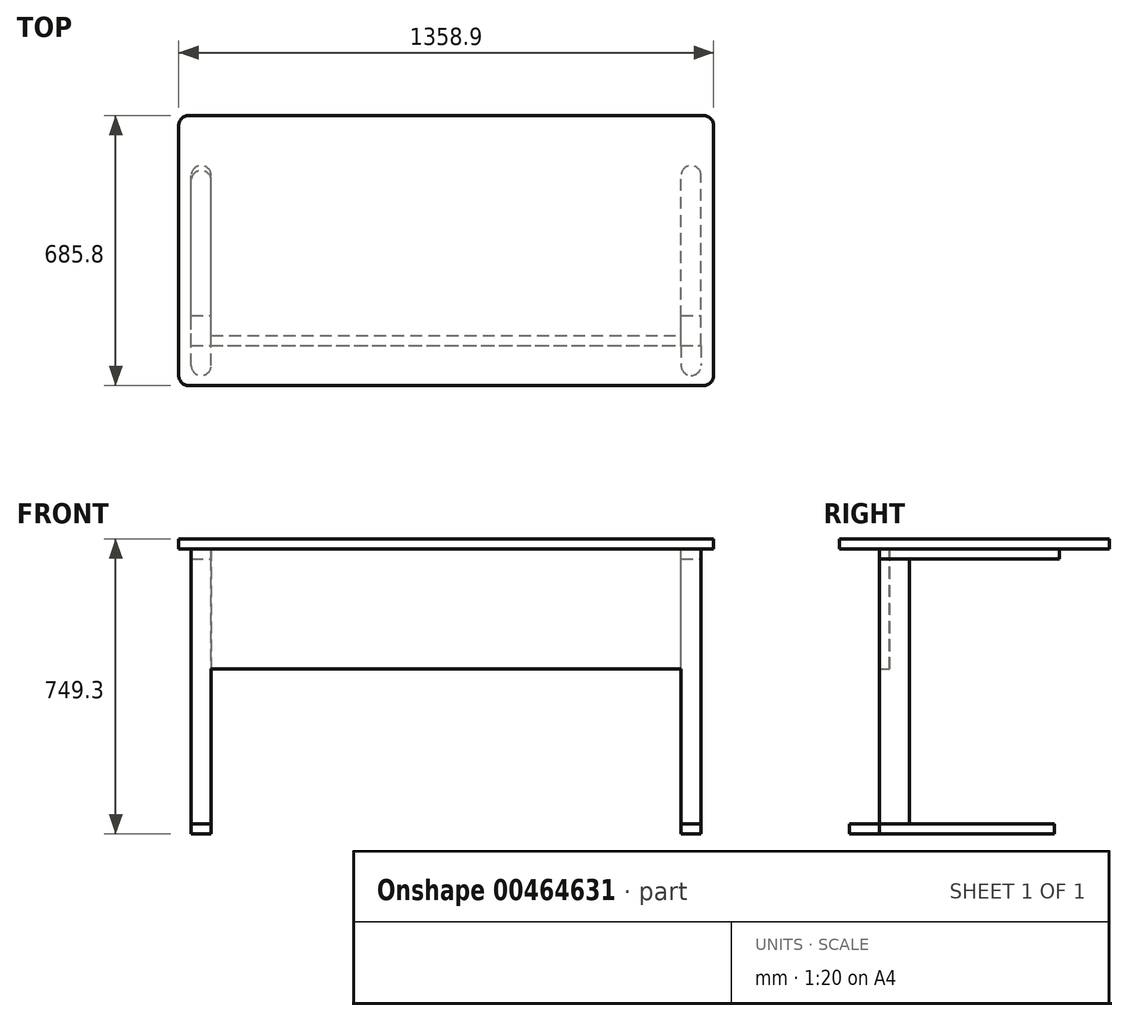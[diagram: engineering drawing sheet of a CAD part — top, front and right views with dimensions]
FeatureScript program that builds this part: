
annotation { "Feature Type Name" : "Feature", "Feature Type Description" : "" }
export const myFeature = defineFeature(function(context is Context, id is Id, definition is map)
    precondition{}
    {
        {
            var Q0;
            Q0=qCreatedBy(makeId("Top.planeOp"),FACE);
            var sketch = newSketch(context, id + "F0", { "sketchPlane" : qUnion([Q0])});
            skLineSegment(sketch, "E0.bottom", {"start": v(-592.93, 685.8) * mm, "end": v(715.17, 685.8) * mm});
            skLineSegment(sketch, "E0.top", {"start": v(-592.93, 0) * mm, "end": v(715.17, 0) * mm});
            skLineSegment(sketch, "E0.left", {"start": v(-618.33, 660.4) * mm, "end": v(-618.33, 25.4) * mm});
            skLineSegment(sketch, "E0.right", {"start": v(740.57, 660.4) * mm, "end": v(740.57, 25.4) * mm});
            skPoint(sketch, "E1.visualSharp", {"position": v(-618.33, 685.8) * mm});
            skArc(sketch, "E1.filletArc", {"start": v(-592.93, 685.8) * mm, "mid": v(-610.9, 678.36) * mm, "end": v(-618.33, 660.4) * mm});
            skPoint(sketch, "E2.visualSharp", {"position": v(740.57, 685.8) * mm});
            skArc(sketch, "E2.filletArc", {"start": v(740.57, 660.4) * mm, "mid": v(733.13, 678.36) * mm, "end": v(715.17, 685.8) * mm});
            skPoint(sketch, "E3.visualSharp", {"position": v(740.57, 0) * mm});
            skArc(sketch, "E3.filletArc", {"start": v(715.17, 0) * mm, "mid": v(733.13, 7.44) * mm, "end": v(740.57, 25.4) * mm});
            skPoint(sketch, "E4.visualSharp", {"position": v(-618.33, 0) * mm});
            skArc(sketch, "E4.filletArc", {"start": v(-618.33, 25.4) * mm, "mid": v(-610.9, 7.44) * mm, "end": v(-592.93, 0) * mm});
            skSolve(sketch);
        }
        {
            var Q0;
            Q0=makeQuery(id+"F0.imprint","IMPRINT",FACE,{"disambiguationData":[TD([[makeQuery(id+"F0.imprint","IMPRINT",EDGE,{"derivedFrom":sQuery(id+"F0.wireOp",EDGE,"E0.bottom")}),-1.0]])]});
            extrude(context, id + "F1", {"entities" : qUnion([Q0]), "depth" : 25.4 * mm});
        }
        {
            var Q0;
            Q0=makeQuery(id+"F1.opExtrude","CAP_FACE",FACE,{"disambiguationData":[OSD([sQuery(id+"F0.wireOp",EDGE,"E0.bottom"),sQuery(id+"F0.wireOp",EDGE,"E0.top"),sQuery(id+"F0.wireOp",EDGE,"E0.left"),sQuery(id+"F0.wireOp",EDGE,"E0.right"),sQuery(id+"F0.wireOp",EDGE,"E1.filletArc"),sQuery(id+"F0.wireOp",EDGE,"E2.filletArc"),sQuery(id+"F0.wireOp",EDGE,"E3.filletArc"),sQuery(id+"F0.wireOp",EDGE,"E4.filletArc")])],"isStart":true});
            var sketch = newSketch(context, id + "F2", { "sketchPlane" : qUnion([Q0])});
            skLineSegment(sketch, "E5.bottom", {"start": v(-586.58, -127) * mm, "end": v(-535.78, -127) * mm});
            skLineSegment(sketch, "E5.top", {"start": v(-561.18, -558.8) * mm, "end": v(-561.18, -558.8) * mm});
            skLineSegment(sketch, "E5.left", {"start": v(-586.58, -127) * mm, "end": v(-586.58, -533.4) * mm});
            skLineSegment(sketch, "E5.right", {"start": v(-535.78, -127) * mm, "end": v(-535.78, -533.4) * mm});
            skLineSegment(sketch, "E6.bottom", {"start": v(658.02, -127) * mm, "end": v(708.82, -127) * mm});
            skLineSegment(sketch, "E6.top", {"start": v(683.42, -558.8) * mm, "end": v(683.42, -558.8) * mm});
            skLineSegment(sketch, "E6.left", {"start": v(658.02, -127) * mm, "end": v(658.02, -533.4) * mm});
            skLineSegment(sketch, "E6.right", {"start": v(708.82, -127) * mm, "end": v(708.82, -533.4) * mm});
            skLineSegment(sketch, "E7.bottom", {"start": v(-586.58, -101.6) * mm, "end": v(-535.78, -101.6) * mm});
            skLineSegment(sketch, "E7.left", {"start": v(-586.58, -101.6) * mm, "end": v(-586.58, -127) * mm});
            skLineSegment(sketch, "E7.right", {"start": v(-535.78, -101.6) * mm, "end": v(-535.78, -127) * mm});
            skLineSegment(sketch, "E8", {"start": v(61.12, 0) * mm, "end": v(61.12, -685.8) * mm});
            skLineSegment(sketch, "E9.MirrorCS", {"start": v(708.82, -127) * mm, "end": v(658.02, -127) * mm});
            skLineSegment(sketch, "E10.MirrorCS", {"start": v(658.02, -101.6) * mm, "end": v(658.02, -127) * mm});
            skLineSegment(sketch, "E11.MirrorCS", {"start": v(708.82, -101.6) * mm, "end": v(708.82, -127) * mm});
            skLineSegment(sketch, "E12.MirrorCS", {"start": v(708.82, -101.6) * mm, "end": v(658.02, -101.6) * mm});
            skPoint(sketch, "E13.visualSharp", {"position": v(-535.78, -558.8) * mm});
            skArc(sketch, "E13.filletArc", {"start": v(-561.18, -558.8) * mm, "mid": v(-543.22, -551.36) * mm, "end": v(-535.78, -533.4) * mm});
            skPoint(sketch, "E14.visualSharp", {"position": v(-586.58, -558.8) * mm});
            skArc(sketch, "E14.filletArc", {"start": v(-586.58, -533.4) * mm, "mid": v(-579.14, -551.36) * mm, "end": v(-561.18, -558.8) * mm});
            skPoint(sketch, "E15.visualSharp", {"position": v(708.82, -558.8) * mm});
            skArc(sketch, "E15.filletArc", {"start": v(683.42, -558.8) * mm, "mid": v(701.38, -551.36) * mm, "end": v(708.82, -533.4) * mm});
            skPoint(sketch, "E16.visualSharp", {"position": v(658.02, -558.8) * mm});
            skArc(sketch, "E16.filletArc", {"start": v(658.02, -533.4) * mm, "mid": v(665.46, -551.36) * mm, "end": v(683.42, -558.8) * mm});
            skSolve(sketch);
        }
        {
            var Q0;
            Q0=makeQuery(id+"F2.imprint","IMPRINT",FACE,{"disambiguationData":[TD([[makeQuery(id+"F2.imprint","IMPRINT",EDGE,{"derivedFrom":sQuery(id+"F2.wireOp",EDGE,"E7.bottom")}),-1.0]])]});
            var Q1;
            {var subQ1=sQuery(id+"F2.wireOp",EDGE,"E5.bottom");Q1=makeQuery(id+"F2.imprint","IMPRINT",FACE,{"disambiguationData":[TD([[makeQuery(id+"F2.imprint","IMPRINT",EDGE,{"derivedFrom":subQ1}),-1.0]])]});}
            var Q2;
            {var subQ1=sQuery(id+"F2.wireOp",EDGE,"E6.left");Q2=makeQuery(id+"F2.imprint","IMPRINT",FACE,{"disambiguationData":[TD([[makeQuery(id+"F2.imprint","IMPRINT",EDGE,{"derivedFrom":subQ1}),1.0]])]});}
            var Q3;
            {var subQ1=sQuery(id+"F2.wireOp",EDGE,"E9.MirrorCS");Q3=makeQuery(id+"F2.imprint","IMPRINT",FACE,{"disambiguationData":[TD([[makeQuery(id+"F2.imprint","IMPRINT",EDGE,{"derivedFrom":subQ1}),-1.0]])]});}
            var Q4;
            Q4=makeQuery(id+"F2.imprint","IMPRINT",FACE,{"disambiguationData":[TD([[makeQuery(id+"F2.imprint","IMPRINT",EDGE,{"derivedFrom":sQuery(id+"F2.wireOp",EDGE,"E5.left")}),1.0]])]});
            var Q5;
            Q5=makeQuery(id+"F2.imprint","IMPRINT",FACE,{"disambiguationData":[TD([[makeQuery(id+"F2.imprint","IMPRINT",EDGE,{"derivedFrom":sQuery(id+"F2.wireOp",EDGE,"E10.MirrorCS")}),1.0]])]});
            extrude(context, id + "F3", {"entities" : qUnion([Q0, Q1, Q2, Q3, Q4, Q5]), "operationType" : NewBodyOperationType.ADD, "depth" : 25.4 * mm});
        }
        {
            var Q0;
            Q0=makeQuery(id+"F3.opExtrude","CAP_FACE",FACE,{"disambiguationData":[OSD([sQuery(id+"F2.wireOp",EDGE,"E5.bottom"),sQuery(id+"F2.wireOp",EDGE,"E5.left"),sQuery(id+"F2.wireOp",EDGE,"E5.right"),sQuery(id+"F2.wireOp",EDGE,"E7.bottom"),sQuery(id+"F2.wireOp",EDGE,"E5.bottom"),sQuery(id+"F2.wireOp",EDGE,"E7.left"),sQuery(id+"F2.wireOp",EDGE,"E7.right"),sQuery(id+"F2.wireOp",EDGE,"E13.filletArc"),sQuery(id+"F2.wireOp",EDGE,"E14.filletArc")])],"isStart":false});
            var sketch = newSketch(context, id + "F4", { "sketchPlane" : qUnion([Q0])});
            skLineSegment(sketch, "E17.bottom", {"start": v(658.03, -101.6) * mm, "end": v(708.76, -101.6) * mm});
            skLineSegment(sketch, "E17.top", {"start": v(658.03, -177.8) * mm, "end": v(708.76, -177.8) * mm});
            skLineSegment(sketch, "E17.left", {"start": v(658.03, -101.6) * mm, "end": v(658.03, -177.8) * mm});
            skLineSegment(sketch, "E17.right", {"start": v(708.76, -101.6) * mm, "end": v(708.76, -177.8) * mm});
            skLineSegment(sketch, "E18.bottom", {"start": v(-586.58, -101.6) * mm, "end": v(-535.78, -101.6) * mm});
            skLineSegment(sketch, "E18.top", {"start": v(-586.58, -177.8) * mm, "end": v(-535.78, -177.8) * mm});
            skLineSegment(sketch, "E18.left", {"start": v(-586.58, -101.6) * mm, "end": v(-586.58, -177.8) * mm});
            skLineSegment(sketch, "E18.right", {"start": v(-535.78, -101.6) * mm, "end": v(-535.78, -177.8) * mm});
            skLineSegment(sketch, "E19.bottom", {"start": v(-535.78, -101.6) * mm, "end": v(658.03, -101.6) * mm});
            skLineSegment(sketch, "E19.top", {"start": v(-535.78, -127) * mm, "end": v(658.03, -127) * mm});
            skLineSegment(sketch, "E19.left", {"start": v(-535.78, -101.6) * mm, "end": v(-535.78, -127) * mm});
            skLineSegment(sketch, "E19.right", {"start": v(658.03, -101.6) * mm, "end": v(658.03, -127) * mm});
            skSolve(sketch);
        }
        {
            var Q0;
            Q0=makeQuery(id+"F4.imprint","IMPRINT",FACE,{"disambiguationData":[TD([[makeQuery(id+"F4.imprint","IMPRINT",EDGE,{"derivedFrom":sQuery(id+"F4.wireOp",EDGE,"E18.bottom")}),-1.0]])]});
            var Q1;
            Q1=makeQuery(id+"F4.imprint","IMPRINT",FACE,{"disambiguationData":[TD([[makeQuery(id+"F4.imprint","IMPRINT",EDGE,{"derivedFrom":sQuery(id+"F4.wireOp",EDGE,"E17.bottom")}),-1.0]])]});
            extrude(context, id + "F5", {"entities" : qUnion([Q0, Q1]), "operationType" : NewBodyOperationType.ADD, "depth" : 673.1 * mm});
        }
        {
            var Q0;
            Q0=makeQuery(id+"F4.imprint","IMPRINT",FACE,{"disambiguationData":[TD([[makeQuery(id+"F4.imprint","IMPRINT",EDGE,{"derivedFrom":sQuery(id+"F4.wireOp",EDGE,"E19.bottom")}),-1.0]])]});
            var sketch = newSketch(context, id + "F6", { "sketchPlane" : qUnion([Q0])});
            skLineSegment(sketch, "E20.bottom", {"start": v(-535.78, -101.6) * mm, "end": v(658.03, -101.6) * mm});
            skLineSegment(sketch, "E20.top", {"start": v(-535.78, -127) * mm, "end": v(658.03, -127) * mm});
            skLineSegment(sketch, "E20.left", {"start": v(-535.78, -101.6) * mm, "end": v(-535.78, -127) * mm});
            skLineSegment(sketch, "E20.right", {"start": v(658.03, -101.6) * mm, "end": v(658.03, -127) * mm});
            skSolve(sketch);
        }
        {
            var Q0;
            Q0=makeQuery(id+"F4.imprint","IMPRINT",FACE,{"disambiguationData":[TD([[makeQuery(id+"F4.imprint","IMPRINT",EDGE,{"derivedFrom":sQuery(id+"F4.wireOp",EDGE,"E19.bottom")}),-1.0]])]});
            extrude(context, id + "F7", {"entities" : qUnion([Q0]), "operationType" : NewBodyOperationType.ADD, "oppositeDirection" : true, "depth" : 25.4 * mm});
        }
        {
            var Q0;
            Q0=makeQuery(id+"F4.imprint","IMPRINT",FACE,{"disambiguationData":[TD([[makeQuery(id+"F4.imprint","IMPRINT",EDGE,{"derivedFrom":sQuery(id+"F4.wireOp",EDGE,"E19.bottom")}),-1.0]])]});
            extrude(context, id + "F8", {"entities" : qUnion([Q0]), "operationType" : NewBodyOperationType.ADD, "depth" : 279.4 * mm});
        }
        {
            var Q0;
            Q0=makeQuery(id+"F5.opExtrude","CAP_FACE",FACE,{"disambiguationData":[OSD([sQuery(id+"F4.wireOp",EDGE,"E17.bottom"),sQuery(id+"F4.wireOp",EDGE,"E17.top"),sQuery(id+"F4.wireOp",EDGE,"E17.left"),sQuery(id+"F4.wireOp",EDGE,"E17.right"),sQuery(id+"F4.wireOp",EDGE,"E19.right")])],"isStart":false});
            var sketch = newSketch(context, id + "F9", { "sketchPlane" : qUnion([Q0])});
            skLineSegment(sketch, "E21.bottom", {"start": v(658.03, -101.6) * mm, "end": v(708.76, -101.6) * mm});
            skLineSegment(sketch, "E21.top", {"start": v(658.03, -101.6) * mm, "end": v(708.76, -101.6) * mm});
            skLineSegment(sketch, "E21.left", {"start": v(658.03, -101.6) * mm, "end": v(658.03, -101.6) * mm});
            skLineSegment(sketch, "E21.right", {"start": v(708.76, -101.6) * mm, "end": v(708.76, -101.6) * mm});
            skLineSegment(sketch, "E22.bottom", {"start": v(658.03, -101.6) * mm, "end": v(708.82, -101.6) * mm});
            skLineSegment(sketch, "E22.top", {"start": v(683.42, -25.4) * mm, "end": v(683.43, -25.4) * mm});
            skLineSegment(sketch, "E22.left", {"start": v(658.03, -101.6) * mm, "end": v(658.03, -50.8) * mm});
            skLineSegment(sketch, "E22.right", {"start": v(708.82, -101.6) * mm, "end": v(708.82, -50.8) * mm});
            skLineSegment(sketch, "E23.top", {"start": v(683.36, -546.1) * mm, "end": v(683.43, -546.1) * mm});
            skLineSegment(sketch, "E23.left", {"start": v(658.03, -101.6) * mm, "end": v(658.03, -520.7) * mm});
            skLineSegment(sketch, "E23.right", {"start": v(708.76, -101.6) * mm, "end": v(708.76, -520.7) * mm});
            skPoint(sketch, "E24.visualSharp", {"position": v(658.03, -25.4) * mm});
            skArc(sketch, "E24.filletArc", {"start": v(683.43, -25.4) * mm, "mid": v(665.47, -32.84) * mm, "end": v(658.03, -50.8) * mm});
            skPoint(sketch, "E25.visualSharp", {"position": v(658.03, -546.1) * mm});
            skArc(sketch, "E25.filletArc", {"start": v(658.03, -520.7) * mm, "mid": v(665.47, -538.66) * mm, "end": v(683.43, -546.1) * mm});
            skPoint(sketch, "E26.visualSharp", {"position": v(708.82, -25.4) * mm});
            skArc(sketch, "E26.filletArc", {"start": v(708.82, -50.8) * mm, "mid": v(701.38, -32.84) * mm, "end": v(683.42, -25.4) * mm});
            skPoint(sketch, "E27.visualSharp", {"position": v(708.76, -546.1) * mm});
            skArc(sketch, "E27.filletArc", {"start": v(683.36, -546.1) * mm, "mid": v(701.32, -538.66) * mm, "end": v(708.76, -520.7) * mm});
            skLineSegment(sketch, "E28", {"start": v(61.12, 0) * mm, "end": v(61.12, -685.65) * mm});
            skLineSegment(sketch, "E29.top", {"start": v(658.03, -177.8) * mm, "end": v(708.76, -177.8) * mm});
            skLineSegment(sketch, "E29.left", {"start": v(658.03, -101.6) * mm, "end": v(658.03, -177.8) * mm});
            skLineSegment(sketch, "E29.right", {"start": v(708.76, -101.6) * mm, "end": v(708.76, -177.8) * mm});
            skLineSegment(sketch, "E30.left", {"start": v(658.03, -177.8) * mm, "end": v(658.03, -520.7) * mm});
            skLineSegment(sketch, "E30.right", {"start": v(708.76, -177.8) * mm, "end": v(708.76, -520.7) * mm});
            skSolve(sketch);
        }
        {
            var Q0;
            Q0=makeQuery(id+"F9.imprint","IMPRINT",FACE,{"disambiguationData":[TD([[makeQuery(id+"F9.imprint","IMPRINT",EDGE,{"derivedFrom":sQuery(id+"F9.wireOp",EDGE,"E29.top")}),-1.0]])]});
            var Q1;
            {var subQ0=sQuery(id+"F9.wireOp",EDGE,"E29.left");Q1=makeQuery(id+"F9.imprint","IMPRINT",FACE,{"disambiguationData":[TD([[makeQuery(id+"F9.imprint","IMPRINT",EDGE,{"derivedFrom":subQ0}),1.0]])]});}
            var Q2;
            {var subQ1=sQuery(id+"F9.wireOp",EDGE,"E22.left");Q2=makeQuery(id+"F9.imprint","IMPRINT",FACE,{"disambiguationData":[TD([[makeQuery(id+"F9.imprint","IMPRINT",EDGE,{"derivedFrom":subQ1}),-1.0]])]});}
            extrude(context, id + "F10", {"entities" : qUnion([Q0, Q1, Q2]), "operationType" : NewBodyOperationType.ADD, "depth" : 25.4 * mm});
        }
        {
            var Q0;
            Q0=makeQuery(id+"F5.opExtrude","CAP_FACE",FACE,{"disambiguationData":[OSD([sQuery(id+"F4.wireOp",EDGE,"E18.bottom"),sQuery(id+"F4.wireOp",EDGE,"E18.top"),sQuery(id+"F4.wireOp",EDGE,"E18.left"),sQuery(id+"F4.wireOp",EDGE,"E18.right"),sQuery(id+"F4.wireOp",EDGE,"E19.left")])],"isStart":false});
            var sketch = newSketch(context, id + "F11", { "sketchPlane" : qUnion([Q0])});
            skPoint(sketch, "E31.oppositeSnap0", {"position": v(-535.78, -139.7) * mm});
            skLineSegment(sketch, "E31.bottom", {"start": v(-561.18, -25.4) * mm, "end": v(-561.18, -25.4) * mm});
            skLineSegment(sketch, "E31.top", {"start": v(-561.18, -546.1) * mm, "end": v(-561.18, -546.1) * mm});
            skLineSegment(sketch, "E31.left", {"start": v(-586.58, -50.8) * mm, "end": v(-586.58, -520.7) * mm});
            skLineSegment(sketch, "E31.right", {"start": v(-535.78, -50.8) * mm, "end": v(-535.78, -520.7) * mm});
            skPoint(sketch, "E32.visualSharp", {"position": v(-535.78, -25.4) * mm});
            skArc(sketch, "E32.filletArc", {"start": v(-535.78, -50.8) * mm, "mid": v(-543.22, -32.84) * mm, "end": v(-561.18, -25.4) * mm});
            skPoint(sketch, "E33.visualSharp", {"position": v(-586.58, -25.4) * mm});
            skArc(sketch, "E33.filletArc", {"start": v(-561.18, -25.4) * mm, "mid": v(-579.14, -32.84) * mm, "end": v(-586.58, -50.8) * mm});
            skPoint(sketch, "E34.visualSharp", {"position": v(-535.78, -546.1) * mm});
            skArc(sketch, "E34.filletArc", {"start": v(-561.18, -546.1) * mm, "mid": v(-543.22, -538.66) * mm, "end": v(-535.78, -520.7) * mm});
            skPoint(sketch, "E35.visualSharp", {"position": v(-586.58, -546.1) * mm});
            skArc(sketch, "E35.filletArc", {"start": v(-586.58, -520.7) * mm, "mid": v(-579.14, -538.66) * mm, "end": v(-561.18, -546.1) * mm});
            skSolve(sketch);
        }
        {
            var Q0;
            {var subQ1=sQuery(id+"F11.wireOp",EDGE,"E32.filletArc");Q0=makeQuery(id+"F11.imprint","IMPRINT",FACE,{"disambiguationData":[TD([[makeQuery(id+"F11.imprint","IMPRINT",EDGE,{"derivedFrom":subQ1}),1.0]])]});}
            var Q1;
            {var subQ1=makeQuery(id+"F5.opExtrude","CAP_EDGE",EDGE,{"disambiguationData":[OSD([sQuery(id+"F4.wireOp",EDGE,"E18.bottom")])],"isStart":false});Q1=makeQuery(id+"F11.imprint","IMPRINT",FACE,{"disambiguationData":[TD([[makeQuery(id+"F11.imprint","IMPRINT",EDGE,{"derivedFrom":subQ1}),-1.0]])]});}
            var Q2;
            {var subQ0=sQuery(id+"F11.wireOp",EDGE,"E34.filletArc");Q2=makeQuery(id+"F11.imprint","IMPRINT",FACE,{"disambiguationData":[TD([[makeQuery(id+"F11.imprint","IMPRINT",EDGE,{"derivedFrom":subQ0}),1.0]])]});}
            extrude(context, id + "F12", {"entities" : qUnion([Q0, Q1, Q2]), "operationType" : NewBodyOperationType.ADD, "depth" : 25.4 * mm});
        }
    });
